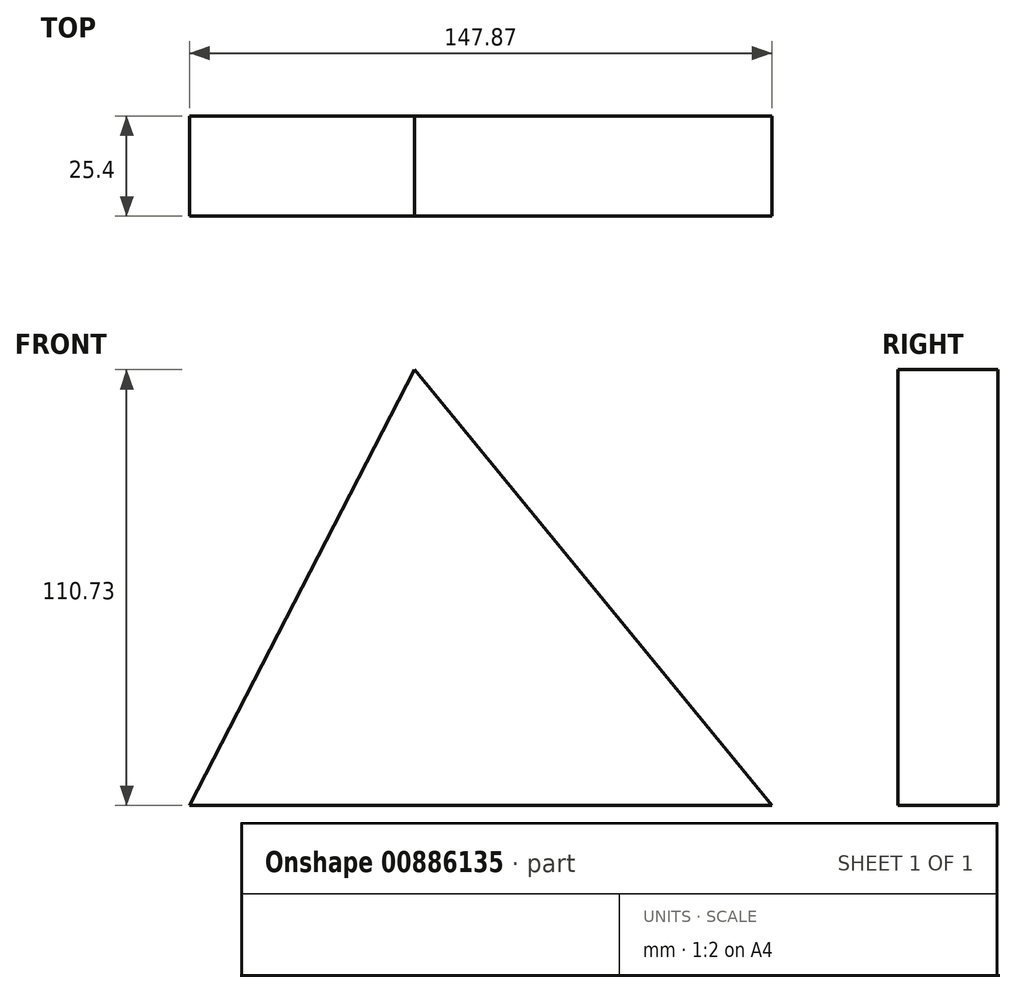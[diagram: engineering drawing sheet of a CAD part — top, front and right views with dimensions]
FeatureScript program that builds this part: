
annotation { "Feature Type Name" : "Feature", "Feature Type Description" : "" }
export const myFeature = defineFeature(function(context is Context, id is Id, definition is map)
    precondition{}
    {
        {
            var Q0;
            Q0=qCreatedBy(makeId("Front.planeOp"),FACE);
            var sketch = newSketch(context, id + "F0", { "sketchPlane" : qUnion([Q0])});
            skLineSegment(sketch, "E0", {"start": v(-28.75, 94.23) * mm, "end": v(61.96, -16.5) * mm});
            skLineSegment(sketch, "E1", {"start": v(61.96, -16.5) * mm, "end": v(-85.91, -16.5) * mm});
            skLineSegment(sketch, "E2", {"start": v(-85.91, -16.5) * mm, "end": v(-28.75, 94.23) * mm});
            skSolve(sketch);
        }
        {
            var Q0;
            Q0=makeQuery(id+"F0.imprint","IMPRINT",FACE,{"disambiguationData":[TD([[makeQuery(id+"F0.imprint","IMPRINT",EDGE,{"derivedFrom":sQuery(id+"F0.wireOp",EDGE,"E0")}),-1.0]])]});
            extrude(context, id + "F1", {"entities" : qUnion([Q0]), "depth" : 25.4 * mm, "offsetDistance" : 25.4 * mm});
        }
    });
